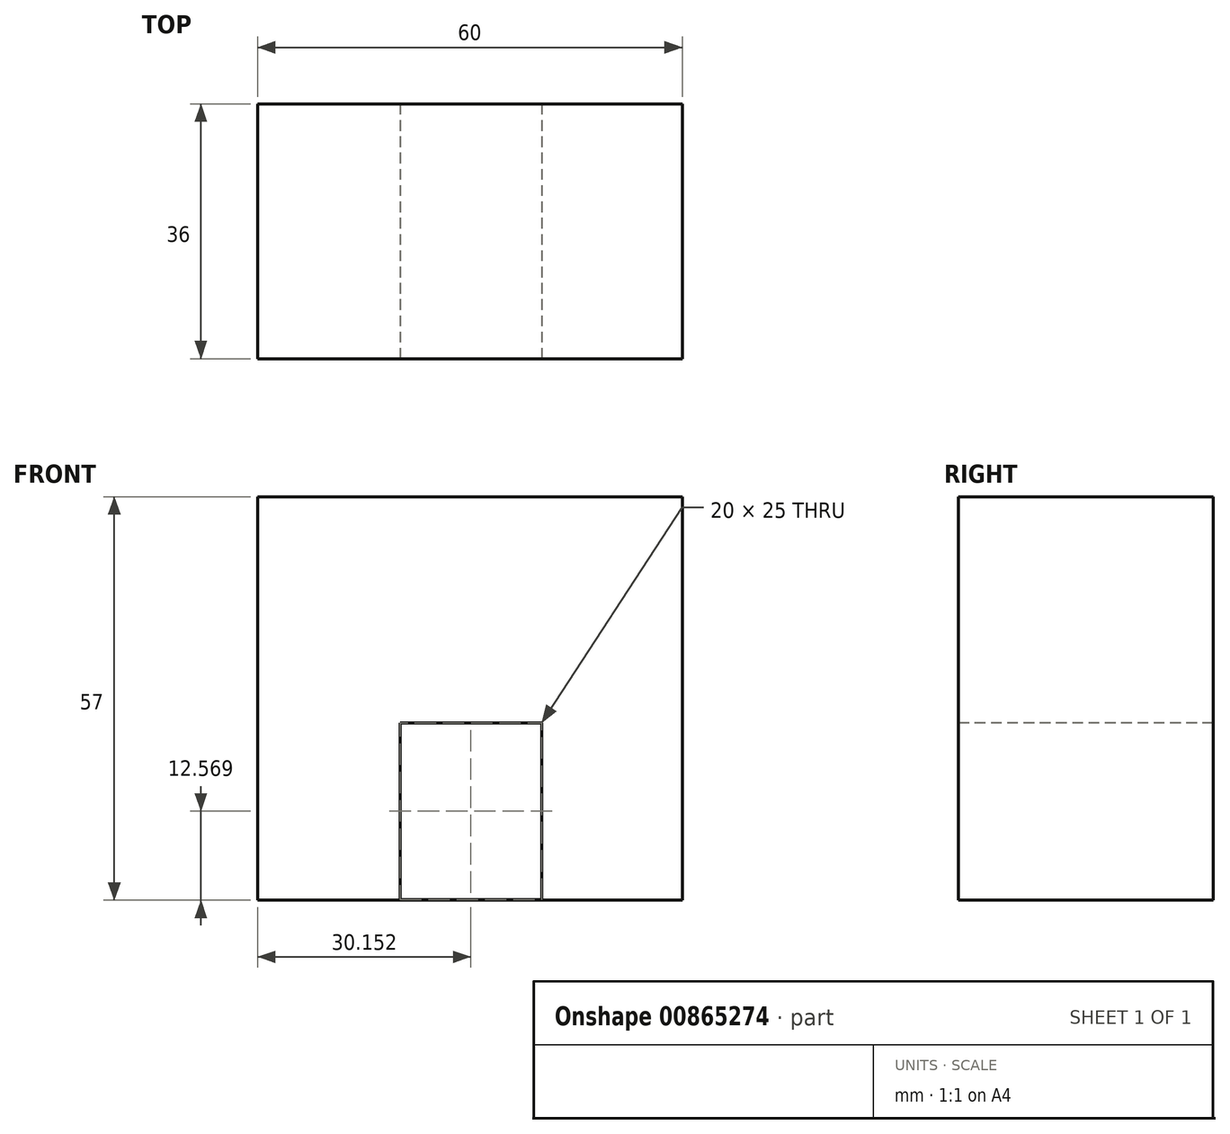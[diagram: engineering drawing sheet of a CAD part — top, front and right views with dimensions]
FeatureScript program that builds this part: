
annotation { "Feature Type Name" : "Feature", "Feature Type Description" : "" }
export const myFeature = defineFeature(function(context is Context, id is Id, definition is map)
    precondition{}
    {
        {
            var Q0;
            Q0=qCreatedBy(makeId("Front.planeOp"),FACE);
            var sketch = newSketch(context, id + "F0", { "sketchPlane" : qUnion([Q0])});
            skLineSegment(sketch, "E0.bottom", {"start": v(30, 28.5) * mm, "end": v(-30, 28.5) * mm});
            skLineSegment(sketch, "E0.top", {"start": v(30, -28.5) * mm, "end": v(-30, -28.5) * mm});
            skLineSegment(sketch, "E0.left", {"start": v(30, 28.5) * mm, "end": v(30, -28.5) * mm});
            skLineSegment(sketch, "E0.right", {"start": v(-30, 28.5) * mm, "end": v(-30, -28.5) * mm});
            skPoint(sketch, "E0.middle", {"position": v(0, 0) * mm});
            skLineSegment(sketch, "E1.bottom", {"start": v(-30, 28.5) * mm, "end": v(-12, 28.5) * mm});
            skLineSegment(sketch, "E1.top", {"start": v(-30, 40.5) * mm, "end": v(-12, 40.5) * mm});
            skLineSegment(sketch, "E1.left", {"start": v(-30, 28.5) * mm, "end": v(-30, 40.5) * mm});
            skLineSegment(sketch, "E1.right", {"start": v(-12, 28.5) * mm, "end": v(-12, 40.5) * mm});
            skLineSegment(sketch, "E2.bottom", {"start": v(30, 28.5) * mm, "end": v(12, 28.5) * mm});
            skLineSegment(sketch, "E2.top", {"start": v(30, 40.5) * mm, "end": v(12, 40.5) * mm});
            skLineSegment(sketch, "E2.left", {"start": v(30, 28.5) * mm, "end": v(30, 40.5) * mm});
            skLineSegment(sketch, "E2.right", {"start": v(12, 28.5) * mm, "end": v(12, 40.5) * mm});
            skLineSegment(sketch, "E3.bottom", {"start": v(10, -3.94) * mm, "end": v(-10, -3.94) * mm});
            skLineSegment(sketch, "E3.top", {"start": v(10, -28.94) * mm, "end": v(-10, -28.94) * mm});
            skLineSegment(sketch, "E3.left", {"start": v(10, -3.94) * mm, "end": v(10, -28.94) * mm});
            skLineSegment(sketch, "E3.right", {"start": v(-10, -3.94) * mm, "end": v(-10, -28.94) * mm});
            skPoint(sketch, "E3.middle", {"position": v(0, -16.44) * mm});
            skSolve(sketch);
        }
        {
            var Q0;
            Q0=makeQuery(id+"F0.imprint","IMPRINT",FACE,{"disambiguationData":[TD([[makeQuery(id+"F0.imprint","IMPRINT",EDGE,{"derivedFrom":sQuery(id+"F0.wireOp",EDGE,"E0.bottom")}),1.0]])]});
            var Q1;
            {var subQ5=sQuery(id+"F0.wireOp",EDGE,"E3.bottom");Q1=makeQuery(id+"F0.imprint","IMPRINT",FACE,{"disambiguationData":[TD([[makeQuery(id+"F0.imprint","IMPRINT",EDGE,{"derivedFrom":subQ5}),1.0]])]});}
            var Q2;
            Q2=makeQuery(id+"F0.imprint","IMPRINT",FACE,{"disambiguationData":[TD([[makeQuery(id+"F0.imprint","IMPRINT",EDGE,{"derivedFrom":sQuery(id+"F0.wireOp",EDGE,"E2.bottom")}),-1.0]])]});
            var Q3;
            Q3=makeQuery(id+"F0.imprint","IMPRINT",FACE,{"disambiguationData":[TD([[makeQuery(id+"F0.imprint","IMPRINT",EDGE,{"derivedFrom":sQuery(id+"F0.wireOp",EDGE,"E1.bottom")}),1.0]])]});
            extrude(context, id + "F1", {"entities" : qUnion([Q0, Q1, Q2, Q3]), "depth" : 36 * mm, "offsetDistance" : 25 * mm});
        }
        {
            var Q0;
            Q0=makeQuery(id+"F1.opExtrude","CAP_FACE",FACE,{"disambiguationData":[OSD([sQuery(id+"F0.wireOp",EDGE,"E0.bottom"),sQuery(id+"F0.wireOp",EDGE,"E0.top"),sQuery(id+"F0.wireOp",EDGE,"E0.left"),sQuery(id+"F0.wireOp",EDGE,"E0.right"),sQuery(id+"F0.wireOp",EDGE,"E1.top"),sQuery(id+"F0.wireOp",EDGE,"E1.left"),sQuery(id+"F0.wireOp",EDGE,"E1.right"),sQuery(id+"F0.wireOp",EDGE,"E2.top"),sQuery(id+"F0.wireOp",EDGE,"E2.left"),sQuery(id+"F0.wireOp",EDGE,"E2.right")])],"isStart":false});
            var sketch = newSketch(context, id + "F2", { "sketchPlane" : qUnion([Q0])});
            skPoint(sketch, "E4.middle", {"position": v(0, -28.5) * mm});
            skLineSegment(sketch, "E5.bottom", {"start": v(10.15, -3.43) * mm, "end": v(-9.85, -3.43) * mm});
            skLineSegment(sketch, "E5.top", {"start": v(10.15, -28.43) * mm, "end": v(-9.85, -28.43) * mm});
            skLineSegment(sketch, "E5.left", {"start": v(10.15, -3.43) * mm, "end": v(10.15, -28.43) * mm});
            skLineSegment(sketch, "E5.right", {"start": v(-9.85, -3.43) * mm, "end": v(-9.85, -28.43) * mm});
            skPoint(sketch, "E5.middle", {"position": v(0.15, -15.93) * mm});
            skSolve(sketch);
        }
        {
            var Q0;
            Q0=makeQuery(id+"F2.imprint","IMPRINT",FACE,{"disambiguationData":[TD([[makeQuery(id+"F2.imprint","IMPRINT",EDGE,{"derivedFrom":sQuery(id+"F2.wireOp",EDGE,"E5.bottom")}),1.0]])]});
            extrude(context, id + "F3", {"entities" : qUnion([Q0]), "operationType" : NewBodyOperationType.REMOVE, "endBound" : BoundingType.THROUGH_ALL, "oppositeDirection" : true, "depth" : 25 * mm, "offsetDistance" : 25 * mm});
        }
    });
